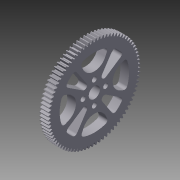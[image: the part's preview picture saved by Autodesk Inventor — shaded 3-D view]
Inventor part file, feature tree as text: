
AUTODESK INVENTOR PART (.ipt)
format: ipt  version: 2012 (Build 160160000, 160)  size: 699,392 bytes
history: native  units: in
note: dims shown in document units (in); Inventor stores cm internally (conversion verified against a paired STEP export)
features: fillet x3, extrude x2, pattern_circular x2, sketch x2, imported_body x1
ambient origin geometry x8: Origin, YZ Plane, XZ Plane, XY Plane, X Axis, Y Axis, Z Axis, Center Point
bodies: Solid1 (feature_tree)
feature tree (10):
  imported_body  "Base1"
  extrude  "Extrusion1"  Depth=0.25in
  fillet  "Fillet1"  Radius=0.0344in
  pattern_circular  "Circular Pattern1"  [2 undecoded]
  fillet  "Fillet2"  Radius=0.0344in
  extrude  "Extrusion2"  Depth=0.0787in
  fillet  "Fillet3"  Radius=0.125in
  pattern_circular  "Circular Pattern2"  [2 undecoded]
  sketch  "Sketch1"  dims[d0=0.125in d1=0.25in d2=0.0344in]
  sketch  "Sketch2"  dims[d3=0.0344in d4=0.0344in d5=0.0344in d6=0.0787in d7=0.125in d8=0.3937in d9=0.0in d10=0.0787in d11=1.5748in d12=360.0deg d14=0.0787in d15=0.125in d16=0.0687in d17=0.0687in d18=0.341in d19=0.3937in d20=0.0in d21=0.0787in d22=1.5748in d23=360.0deg]
note: 4 required parameter values undecoded (feature->parameter linkage not recoverable at this tier; creation-order binding heuristic only, values carry confidence <= 0.55)
